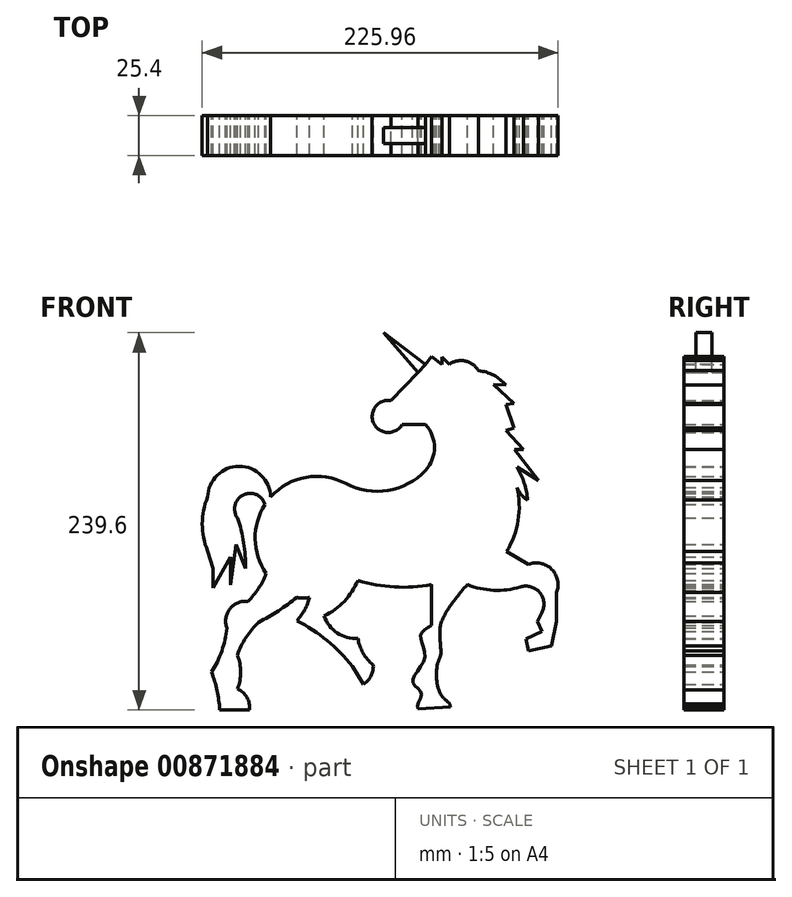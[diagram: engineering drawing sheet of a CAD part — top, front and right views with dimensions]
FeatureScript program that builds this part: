
annotation { "Feature Type Name" : "Feature", "Feature Type Description" : "" }
export const myFeature = defineFeature(function(context is Context, id is Id, definition is map)
    precondition{}
    {
        {
            var Q0;
            Q0=qCreatedBy(makeId("Front.planeOp"),FACE);
            var sketch = newSketch(context, id + "F0", { "sketchPlane" : qUnion([Q0])});
            skLineSegment(sketch, "E0", {"start": v(117.02, 256.9) * mm, "end": v(157.35, 226.79) * mm});
            skLineSegment(sketch, "E1", {"start": v(117.02, 256.9) * mm, "end": v(153.27, 222.2) * mm});
            skLineSegment(sketch, "E2", {"start": v(153.27, 222.2) * mm, "end": v(135.55, 203.69) * mm});
            skArc(sketch, "E3", {"start": v(135.55, 203.69) * mm, "mid": v(124.47, 189.38) * mm, "end": v(142.55, 188.5) * mm});
            skLineSegment(sketch, "E4", {"start": v(142.55, 188.5) * mm, "end": v(157.35, 188.5) * mm});
            skArc(sketch, "E5", {"start": v(157.35, 159.4) * mm, "mid": v(163.1, 173.94) * mm, "end": v(157.35, 188.5) * mm});
            skArc(sketch, "E6", {"start": v(106.85, 151.02) * mm, "mid": v(59.08, 142.48) * mm, "end": v(56.24, 94.04) * mm});
            skArc(sketch, "E7", {"start": v(106.85, 151.02) * mm, "mid": v(133.52, 146.63) * mm, "end": v(157.35, 159.4) * mm});
            skArc(sketch, "E8", {"start": v(208.92, 107.83) * mm, "mid": v(216.22, 127.6) * mm, "end": v(215.55, 148.67) * mm});
            skArc(sketch, "E9", {"start": v(183.9, 86.9) * mm, "mid": v(200.68, 83.25) * mm, "end": v(217.72, 85.39) * mm});
            skArc(sketch, "E10", {"start": v(231.43, 69.23) * mm, "mid": v(229.88, 81.8) * mm, "end": v(217.72, 85.39) * mm});
            skArc(sketch, "E11", {"start": v(240.57, 81.8) * mm, "mid": v(237.5, 96.6) * mm, "end": v(222.7, 99.66) * mm});
            skLineSegment(sketch, "E12", {"start": v(240.57, 81.8) * mm, "end": v(240.57, 63.41) * mm});
            skLineSegment(sketch, "E13", {"start": v(208.92, 107.83) * mm, "end": v(222.7, 99.66) * mm});
            skLineSegment(sketch, "E14", {"start": v(231.43, 69.23) * mm, "end": v(228.56, 63.41) * mm});
            skLineSegment(sketch, "E15", {"start": v(228.56, 63.41) * mm, "end": v(231.43, 57) * mm});
            skLineSegment(sketch, "E16", {"start": v(231.43, 57) * mm, "end": v(221.07, 52.36) * mm});
            skLineSegment(sketch, "E17", {"start": v(221.07, 52.36) * mm, "end": v(222.7, 44.75) * mm});
            skLineSegment(sketch, "E18", {"start": v(222.7, 44.75) * mm, "end": v(237.34, 47.87) * mm});
            skLineSegment(sketch, "E19", {"start": v(237.34, 47.87) * mm, "end": v(240.57, 63.41) * mm});
            skArc(sketch, "E20", {"start": v(59.08, 142.48) * mm, "mid": v(39.04, 161.99) * mm, "end": v(19, 142.48) * mm});
            skPoint(sketch, "E20.endSnap0", {"position": v(59.08, 142.48) * mm});
            skArc(sketch, "E21", {"start": v(55.46, 137.72) * mm, "mid": v(41.7, 143.82) * mm, "end": v(37.88, 129.27) * mm});
            skArc(sketch, "E22", {"start": v(19, 142.48) * mm, "mid": v(15.58, 125.41) * mm, "end": v(19, 108.34) * mm});
            skArc(sketch, "E23", {"start": v(44.52, 76.17) * mm, "mid": v(33.18, 71.46) * mm, "end": v(31.25, 59.33) * mm});
            skArc(sketch, "E24", {"start": v(114.47, 89.45) * mm, "mid": v(137.67, 85.34) * mm, "end": v(161.2, 86.84) * mm});
            skArc(sketch, "E25", {"start": v(93.02, 66.98) * mm, "mid": v(105.8, 76.26) * mm, "end": v(114.47, 89.45) * mm});
            skArc(sketch, "E26", {"start": v(93.02, 66.98) * mm, "mid": v(101.25, 56.1) * mm, "end": v(114.47, 52.69) * mm});
            skArc(sketch, "E27", {"start": v(114.47, 52.69) * mm, "mid": v(117.73, 43.35) * mm, "end": v(124.17, 35.84) * mm});
            skArc(sketch, "E28", {"start": v(118.04, 23.59) * mm, "mid": v(122.8, 28.87) * mm, "end": v(124.17, 35.84) * mm});
            skArc(sketch, "E29", {"start": v(167.05, 61.35) * mm, "mid": v(177.73, 72.64) * mm, "end": v(183.9, 86.9) * mm});
            skArc(sketch, "E30", {"start": v(167.05, 41.98) * mm, "mid": v(169.24, 51.67) * mm, "end": v(167.05, 61.35) * mm});
            skArc(sketch, "E31", {"start": v(167.05, 41.98) * mm, "mid": v(164.24, 29.59) * mm, "end": v(167.05, 17.2) * mm});
            skArc(sketch, "E32", {"start": v(173.17, 9.02) * mm, "mid": v(171.2, 13.93) * mm, "end": v(167.05, 17.2) * mm});
            skLineSegment(sketch, "E33", {"start": v(152.75, 7.8) * mm, "end": v(173.17, 9.02) * mm});
            skLineSegment(sketch, "E34", {"start": v(161.2, 86.84) * mm, "end": v(161.2, 60.95) * mm});
            skFitSpline(sketch, "E35", {"points": [v(161.2, 60.95) * mm, v(154.29, 54.22) * mm, v(156.84, 40.44) * mm, v(149.18, 25.12) * mm, v(154.8, 17.46) * mm, v(152.75, 7.8) * mm, v(173.17, 9.02) * mm, v(167.05, 17.2) * mm, v(167.05, 41.98) * mm, v(167.05, 61.35) * mm, v(183.9, 86.9) * mm], "startDerivative": vector(-126.82, -72.82) * mm, "endDerivative": vector(160.9, 190.3) * mm});
            skArc(sketch, "E36", {"start": v(44.52, 76.17) * mm, "mid": v(51.4, 84.44) * mm, "end": v(56.24, 94.04) * mm});
            skArc(sketch, "E37", {"start": v(21.55, 31.25) * mm, "mid": v(28.01, 44.73) * mm, "end": v(31.25, 59.33) * mm});
            skArc(sketch, "E38", {"start": v(26.65, 7.25) * mm, "mid": v(25.03, 19.45) * mm, "end": v(21.55, 31.25) * mm});
            skLineSegment(sketch, "E39", {"start": v(26.65, 7.25) * mm, "end": v(45.54, 7.25) * mm});
            skArc(sketch, "E40", {"start": v(51.4, 62.9) * mm, "mid": v(63.94, 70.18) * mm, "end": v(75.66, 78.73) * mm});
            skPoint(sketch, "E40.startSnap0", {"position": v(51.4, 84.44) * mm});
            skArc(sketch, "E41", {"start": v(75.66, 78.73) * mm, "mid": v(79.75, 78.22) * mm, "end": v(83.83, 78.73) * mm});
            skArc(sketch, "E42", {"start": v(75.66, 63.92) * mm, "mid": v(80.62, 70.84) * mm, "end": v(83.83, 78.73) * mm});
            skArc(sketch, "E43", {"start": v(110.9, 34.82) * mm, "mid": v(94.88, 51.31) * mm, "end": v(75.66, 63.92) * mm});
            skLineSegment(sketch, "E44", {"start": v(110.9, 34.82) * mm, "end": v(118.04, 23.59) * mm});
            skArc(sketch, "E45", {"start": v(51.4, 62.9) * mm, "mid": v(43.37, 53.26) * mm, "end": v(37.88, 41.97) * mm});
            skArc(sketch, "E46", {"start": v(37.88, 20.52) * mm, "mid": v(39.97, 31.25) * mm, "end": v(37.88, 41.97) * mm});
            skArc(sketch, "E47", {"start": v(45.54, 7.25) * mm, "mid": v(43.99, 15.2) * mm, "end": v(37.88, 20.52) * mm});
            skArc(sketch, "E48", {"start": v(215.55, 148.67) * mm, "mid": v(218.09, 143.95) * mm, "end": v(222.2, 140.5) * mm});
            skArc(sketch, "E49", {"start": v(222.2, 140.5) * mm, "mid": v(220.05, 151.34) * mm, "end": v(215.55, 161.44) * mm});
            skLineSegment(sketch, "E50", {"start": v(157.35, 226.79) * mm, "end": v(161.08, 231.77) * mm});
            skLineSegment(sketch, "E51", {"start": v(161.08, 231.77) * mm, "end": v(167.75, 226.79) * mm});
            skLineSegment(sketch, "E52", {"start": v(167.75, 226.79) * mm, "end": v(167.75, 231.38) * mm});
            skLineSegment(sketch, "E53", {"start": v(167.75, 231.38) * mm, "end": v(172.55, 226.79) * mm});
            skArc(sketch, "E54", {"start": v(191.05, 222.7) * mm, "mid": v(182.7, 228.81) * mm, "end": v(172.55, 226.79) * mm});
            skArc(sketch, "E55", {"start": v(208.4, 213.51) * mm, "mid": v(200.64, 219.82) * mm, "end": v(191.05, 222.7) * mm});
            skLineSegment(sketch, "E56", {"start": v(200.64, 214.02) * mm, "end": v(208.4, 213.51) * mm});
            skPoint(sketch, "E56.startSnap0", {"position": v(200.64, 219.82) * mm});
            skLineSegment(sketch, "E57", {"start": v(200.64, 214.02) * mm, "end": v(213.51, 201.77) * mm});
            skLineSegment(sketch, "E58", {"start": v(213.51, 201.77) * mm, "end": v(208.4, 201.31) * mm});
            skLineSegment(sketch, "E59", {"start": v(208.4, 201.31) * mm, "end": v(213.51, 186.45) * mm});
            skLineSegment(sketch, "E60", {"start": v(213.51, 186.45) * mm, "end": v(208.4, 184.7) * mm});
            skLineSegment(sketch, "E61", {"start": v(208.4, 184.7) * mm, "end": v(219.64, 172.67) * mm});
            skLineSegment(sketch, "E62", {"start": v(219.64, 172.67) * mm, "end": v(214.02, 172.67) * mm});
            skPoint(sketch, "E62.endSnap0", {"position": v(214.02, 178.68) * mm});
            skLineSegment(sketch, "E63", {"start": v(214.02, 172.67) * mm, "end": v(229.08, 152.88) * mm});
            skLineSegment(sketch, "E64", {"start": v(229.08, 152.88) * mm, "end": v(215.55, 161.44) * mm});
            skArc(sketch, "E65", {"start": v(43.12, 97.11) * mm, "mid": v(41.95, 113.43) * mm, "end": v(37.88, 129.27) * mm});
            skLineSegment(sketch, "E66", {"start": v(43.12, 97.11) * mm, "end": v(36.91, 112.47) * mm});
            skLineSegment(sketch, "E67", {"start": v(36.91, 112.47) * mm, "end": v(33.45, 86.7) * mm});
            skLineSegment(sketch, "E68", {"start": v(33.45, 86.7) * mm, "end": v(33.45, 104.26) * mm});
            skLineSegment(sketch, "E69", {"start": v(33.45, 104.26) * mm, "end": v(22.3, 84.75) * mm});
            skLineSegment(sketch, "E70", {"start": v(22.3, 84.75) * mm, "end": v(22.3, 97.11) * mm});
            skLineSegment(sketch, "E71", {"start": v(22.3, 97.11) * mm, "end": v(19, 108.34) * mm});
            skLineSegment(sketch, "E72", {"start": v(153.27, 222.2) * mm, "end": v(157.35, 226.79) * mm});
            skSolve(sketch);
        }
        {
            var Q0;
            {var subQ0=sQuery(id+"F0.wireOp",EDGE,"E20");Q0=makeQuery(id+"F0.imprint","IMPRINT",FACE,{"disambiguationData":[TD([[makeQuery(id+"F0.imprint","IMPRINT",EDGE,{"derivedFrom":subQ0}),1.0]])]});}
            var Q1;
            Q1=makeQuery(id+"F0.imprint","IMPRINT",FACE,{"disambiguationData":[TD([[makeQuery(id+"F0.imprint","IMPRINT",EDGE,{"derivedFrom":sQuery(id+"F0.wireOp",EDGE,"E2")}),1.0]])]});
            extrude(context, id + "F1", {"entities" : qUnion([Q0, Q1]), "depth" : 25.4 * mm, "offsetDistance" : 25.4 * mm});
        }
        {
            var Q0;
            Q0=qCreatedBy(makeId("Front.planeOp"),FACE);
            var sketch = newSketch(context, id + "F2", { "sketchPlane" : qUnion([Q0])});
            skLineSegment(sketch, "E73", {"start": v(152.74, 221.48) * mm, "end": v(130.7, 246.85) * mm});
            skLineSegment(sketch, "E74", {"start": v(157.52, 226.55) * mm, "end": v(130.7, 246.85) * mm});
            skLineSegment(sketch, "E75", {"start": v(152.74, 221.48) * mm, "end": v(157.52, 226.55) * mm});
            skSolve(sketch);
        }
        {
            var Q0;
            Q0=makeQuery(id+"F2.imprint","IMPRINT",FACE,{"disambiguationData":[TD([[makeQuery(id+"F2.imprint","IMPRINT",EDGE,{"derivedFrom":sQuery(id+"F2.wireOp",EDGE,"E73")}),-1.0]])]});
            extrude(context, id + "F3", {"entities" : qUnion([Q0]), "operationType" : NewBodyOperationType.ADD, "depth" : 25.4 * mm, "offsetDistance" : 25.4 * mm});
        }
        {
            var Q0;
            Q0=makeQuery(id+"F3.boolean.opBoolean","MERGE",FACE,{"derivedFrom":[makeQuery(id+"F1.opExtrude","CAP_FACE",FACE,{"disambiguationData":[OSD([sQuery(id+"F0.wireOp",EDGE,"E2"),sQuery(id+"F0.wireOp",EDGE,"E3"),sQuery(id+"F0.wireOp",EDGE,"E4"),sQuery(id+"F0.wireOp",EDGE,"E5"),sQuery(id+"F0.wireOp",EDGE,"E6"),sQuery(id+"F0.wireOp",EDGE,"E7"),sQuery(id+"F0.wireOp",EDGE,"E8"),sQuery(id+"F0.wireOp",EDGE,"E9"),sQuery(id+"F0.wireOp",EDGE,"E10"),sQuery(id+"F0.wireOp",EDGE,"E11"),sQuery(id+"F0.wireOp",EDGE,"E12"),sQuery(id+"F0.wireOp",EDGE,"E13"),sQuery(id+"F0.wireOp",EDGE,"E14"),sQuery(id+"F0.wireOp",EDGE,"E15"),sQuery(id+"F0.wireOp",EDGE,"E16"),sQuery(id+"F0.wireOp",EDGE,"E17"),sQuery(id+"F0.wireOp",EDGE,"E18"),sQuery(id+"F0.wireOp",EDGE,"E19"),sQuery(id+"F0.wireOp",EDGE,"E20"),sQuery(id+"F0.wireOp",EDGE,"E21"),sQuery(id+"F0.wireOp",EDGE,"E22"),sQuery(id+"F0.wireOp",EDGE,"E23"),sQuery(id+"F0.wireOp",EDGE,"E24"),sQuery(id+"F0.wireOp",EDGE,"E25"),sQuery(id+"F0.wireOp",EDGE,"E26"),sQuery(id+"F0.wireOp",EDGE,"E27"),sQuery(id+"F0.wireOp",EDGE,"E28"),sQuery(id+"F0.wireOp",EDGE,"E31"),sQuery(id+"F0.wireOp",EDGE,"E32"),sQuery(id+"F0.wireOp",EDGE,"E33"),sQuery(id+"F0.wireOp",EDGE,"E34"),sQuery(id+"F0.wireOp",EDGE,"E35"),sQuery(id+"F0.wireOp",EDGE,"E36"),sQuery(id+"F0.wireOp",EDGE,"E37"),sQuery(id+"F0.wireOp",EDGE,"E38"),sQuery(id+"F0.wireOp",EDGE,"E39"),sQuery(id+"F0.wireOp",EDGE,"E40"),sQuery(id+"F0.wireOp",EDGE,"E41"),sQuery(id+"F0.wireOp",EDGE,"E42"),sQuery(id+"F0.wireOp",EDGE,"E43"),sQuery(id+"F0.wireOp",EDGE,"E44"),sQuery(id+"F0.wireOp",EDGE,"E45"),sQuery(id+"F0.wireOp",EDGE,"E46"),sQuery(id+"F0.wireOp",EDGE,"E47"),sQuery(id+"F0.wireOp",EDGE,"E48"),sQuery(id+"F0.wireOp",EDGE,"E49"),sQuery(id+"F0.wireOp",EDGE,"E50"),sQuery(id+"F0.wireOp",EDGE,"E51"),sQuery(id+"F0.wireOp",EDGE,"E52"),sQuery(id+"F0.wireOp",EDGE,"E53"),sQuery(id+"F0.wireOp",EDGE,"E54"),sQuery(id+"F0.wireOp",EDGE,"E55"),sQuery(id+"F0.wireOp",EDGE,"E56"),sQuery(id+"F0.wireOp",EDGE,"E57"),sQuery(id+"F0.wireOp",EDGE,"E58"),sQuery(id+"F0.wireOp",EDGE,"E59"),sQuery(id+"F0.wireOp",EDGE,"E60"),sQuery(id+"F0.wireOp",EDGE,"E61"),sQuery(id+"F0.wireOp",EDGE,"E62"),sQuery(id+"F0.wireOp",EDGE,"E63"),sQuery(id+"F0.wireOp",EDGE,"E64"),sQuery(id+"F0.wireOp",EDGE,"E65"),sQuery(id+"F0.wireOp",EDGE,"E66"),sQuery(id+"F0.wireOp",EDGE,"E67"),sQuery(id+"F0.wireOp",EDGE,"E68"),sQuery(id+"F0.wireOp",EDGE,"E69"),sQuery(id+"F0.wireOp",EDGE,"E70"),sQuery(id+"F0.wireOp",EDGE,"E71"),sQuery(id+"F0.wireOp",EDGE,"E72")])],"isStart":true}),makeQuery(id+"F3.opExtrude","CAP_FACE",FACE,{"disambiguationData":[OSD([sQuery(id+"F2.wireOp",EDGE,"E73"),sQuery(id+"F2.wireOp",EDGE,"E74"),sQuery(id+"F2.wireOp",EDGE,"E75")])],"isStart":true})]});
            var sketch = newSketch(context, id + "F4", { "sketchPlane" : qUnion([Q0])});
            skLineSegment(sketch, "E76", {"start": v(-152.67, 221.56) * mm, "end": v(-157.3, 226.72) * mm});
            skLineSegment(sketch, "E77", {"start": v(-157.3, 226.72) * mm, "end": v(-130.7, 246.85) * mm});
            skLineSegment(sketch, "E78", {"start": v(-130.7, 246.85) * mm, "end": v(-152.67, 221.56) * mm});
            skSolve(sketch);
        }
        {
            var Q0;
            Q0=makeQuery(id+"F4.imprint","IMPRINT",FACE,{"disambiguationData":[TD([[makeQuery(id+"F4.imprint","IMPRINT",EDGE,{"derivedFrom":sQuery(id+"F4.wireOp",EDGE,"E76")}),-1.0]])]});
            extrude(context, id + "F5", {"entities" : qUnion([Q0]), "operationType" : NewBodyOperationType.REMOVE, "oppositeDirection" : true, "depth" : 7.62 * mm, "offsetDistance" : 25.4 * mm});
        }
        {
            var Q0;
            Q0=makeQuery(id+"F3.boolean.opBoolean","MERGE",FACE,{"derivedFrom":[makeQuery(id+"F1.opExtrude","CAP_FACE",FACE,{"disambiguationData":[OSD([sQuery(id+"F0.wireOp",EDGE,"E2"),sQuery(id+"F0.wireOp",EDGE,"E3"),sQuery(id+"F0.wireOp",EDGE,"E4"),sQuery(id+"F0.wireOp",EDGE,"E5"),sQuery(id+"F0.wireOp",EDGE,"E6"),sQuery(id+"F0.wireOp",EDGE,"E7"),sQuery(id+"F0.wireOp",EDGE,"E8"),sQuery(id+"F0.wireOp",EDGE,"E9"),sQuery(id+"F0.wireOp",EDGE,"E10"),sQuery(id+"F0.wireOp",EDGE,"E11"),sQuery(id+"F0.wireOp",EDGE,"E12"),sQuery(id+"F0.wireOp",EDGE,"E13"),sQuery(id+"F0.wireOp",EDGE,"E14"),sQuery(id+"F0.wireOp",EDGE,"E15"),sQuery(id+"F0.wireOp",EDGE,"E16"),sQuery(id+"F0.wireOp",EDGE,"E17"),sQuery(id+"F0.wireOp",EDGE,"E18"),sQuery(id+"F0.wireOp",EDGE,"E19"),sQuery(id+"F0.wireOp",EDGE,"E20"),sQuery(id+"F0.wireOp",EDGE,"E21"),sQuery(id+"F0.wireOp",EDGE,"E22"),sQuery(id+"F0.wireOp",EDGE,"E23"),sQuery(id+"F0.wireOp",EDGE,"E24"),sQuery(id+"F0.wireOp",EDGE,"E25"),sQuery(id+"F0.wireOp",EDGE,"E26"),sQuery(id+"F0.wireOp",EDGE,"E27"),sQuery(id+"F0.wireOp",EDGE,"E28"),sQuery(id+"F0.wireOp",EDGE,"E31"),sQuery(id+"F0.wireOp",EDGE,"E32"),sQuery(id+"F0.wireOp",EDGE,"E33"),sQuery(id+"F0.wireOp",EDGE,"E34"),sQuery(id+"F0.wireOp",EDGE,"E35"),sQuery(id+"F0.wireOp",EDGE,"E36"),sQuery(id+"F0.wireOp",EDGE,"E37"),sQuery(id+"F0.wireOp",EDGE,"E38"),sQuery(id+"F0.wireOp",EDGE,"E39"),sQuery(id+"F0.wireOp",EDGE,"E40"),sQuery(id+"F0.wireOp",EDGE,"E41"),sQuery(id+"F0.wireOp",EDGE,"E42"),sQuery(id+"F0.wireOp",EDGE,"E43"),sQuery(id+"F0.wireOp",EDGE,"E44"),sQuery(id+"F0.wireOp",EDGE,"E45"),sQuery(id+"F0.wireOp",EDGE,"E46"),sQuery(id+"F0.wireOp",EDGE,"E47"),sQuery(id+"F0.wireOp",EDGE,"E48"),sQuery(id+"F0.wireOp",EDGE,"E49"),sQuery(id+"F0.wireOp",EDGE,"E50"),sQuery(id+"F0.wireOp",EDGE,"E51"),sQuery(id+"F0.wireOp",EDGE,"E52"),sQuery(id+"F0.wireOp",EDGE,"E53"),sQuery(id+"F0.wireOp",EDGE,"E54"),sQuery(id+"F0.wireOp",EDGE,"E55"),sQuery(id+"F0.wireOp",EDGE,"E56"),sQuery(id+"F0.wireOp",EDGE,"E57"),sQuery(id+"F0.wireOp",EDGE,"E58"),sQuery(id+"F0.wireOp",EDGE,"E59"),sQuery(id+"F0.wireOp",EDGE,"E60"),sQuery(id+"F0.wireOp",EDGE,"E61"),sQuery(id+"F0.wireOp",EDGE,"E62"),sQuery(id+"F0.wireOp",EDGE,"E63"),sQuery(id+"F0.wireOp",EDGE,"E64"),sQuery(id+"F0.wireOp",EDGE,"E65"),sQuery(id+"F0.wireOp",EDGE,"E66"),sQuery(id+"F0.wireOp",EDGE,"E67"),sQuery(id+"F0.wireOp",EDGE,"E68"),sQuery(id+"F0.wireOp",EDGE,"E69"),sQuery(id+"F0.wireOp",EDGE,"E70"),sQuery(id+"F0.wireOp",EDGE,"E71"),sQuery(id+"F0.wireOp",EDGE,"E72")])],"isStart":false}),makeQuery(id+"F3.opExtrude","CAP_FACE",FACE,{"disambiguationData":[OSD([sQuery(id+"F2.wireOp",EDGE,"E73"),sQuery(id+"F2.wireOp",EDGE,"E74"),sQuery(id+"F2.wireOp",EDGE,"E75")])],"isStart":false})]});
            var sketch = newSketch(context, id + "F6", { "sketchPlane" : qUnion([Q0])});
            skLineSegment(sketch, "E79", {"start": v(152.67, 221.56) * mm, "end": v(157.35, 226.79) * mm});
            skLineSegment(sketch, "E80", {"start": v(157.35, 226.79) * mm, "end": v(130.7, 246.85) * mm});
            skSolve(sketch);
        }
        {
            var Q0;
            {var subQ1=makeQuery(id+"F3.opExtrude","CAP_EDGE",EDGE,{"disambiguationData":[OSD([sQuery(id+"F2.wireOp",EDGE,"E73")])],"isStart":false});Q0=makeQuery(id+"F6.imprint","IMPRINT",FACE,{"disambiguationData":[TD([[makeQuery(id+"F6.imprint","IMPRINT",EDGE,{"derivedFrom":subQ1}),-1.0]])]});}
            extrude(context, id + "F7", {"entities" : qUnion([Q0]), "operationType" : NewBodyOperationType.REMOVE, "oppositeDirection" : true, "depth" : 7.62 * mm, "offsetDistance" : 25.4 * mm});
        }
    });
